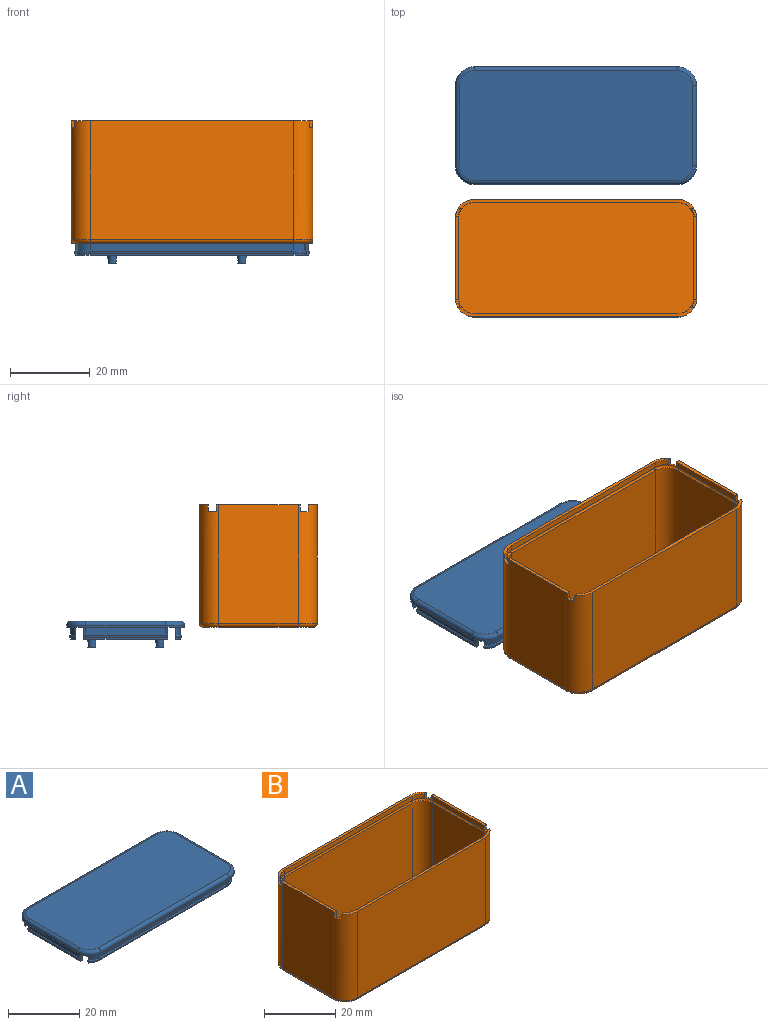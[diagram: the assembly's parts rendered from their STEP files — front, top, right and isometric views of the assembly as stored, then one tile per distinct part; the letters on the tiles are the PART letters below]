
ASSEMBLY  parts=2 mates=1
PART A: 82 faces, bbox 61.3x30.3x6.5 mm
  f0: torus R=3.75mm, axis (0,0,1), area 0.5mm2, adj f14,f15,f20,f68
  f1: torus R=3.75mm, axis (0,0,1), area 0.5mm2, adj f13,f16,f24,f67
  f2: torus R=3.75mm, axis (0,0,1), area 3.3mm2, adj f12,f17,f19,f65
  f3: torus R=3.75mm, axis (0,0,1), area 3.3mm2, adj f11,f18,f19,f62
  f4: cylinder r=3mm len=3mm, axis (0,0,1), area 1.5mm2, adj f10,f27,f50,f68
  f5: cylinder r=3mm len=3mm, axis (0,0,1), area 1.5mm2, adj f9,f31,f50,f67
  f6: cylinder r=3mm len=3mm, axis (0,0,1), area 5.3mm2, adj f8,f33,f50,f65
  f7: cylinder r=3mm len=3mm, axis (0,0,1), area 5.3mm2, adj f8,f33,f50,f62
  f8: plane 56.59x1.25mm, normal (0,0,-1), area 42mm2, adj f6,f7,f11,f12,f33,f38,f62,f65
  f9: plane 21x0.79mm, normal (0,0,-1), area 15.8mm2, adj f5,f13,f31,f32,f39,f40,f64,f67
  f10: plane 21x0.79mm, normal (0,0,-1), area 15.8mm2, adj f4,f14,f27,f34,f36,f37,f63,f68
  f11: cylinder r=3.75mm len=2.8mm, axis (0,0,1), area 1.4mm2, adj f3,f8,f38,f62
  f12: cylinder r=3.75mm len=2.8mm, axis (0,0,1), area 1.4mm2, adj f2,f8,f38,f65
  f13: cylinder r=3.75mm len=0.5mm, axis (0,0,1), area 0.2mm2, adj f1,f9,f40,f67
  f14: cylinder r=3.75mm len=0.5mm, axis (0,0,1), area 0.2mm2, adj f0,f10,f36,f68
  f15: cylinder r=3.75mm len=1.95mm, axis (0,0,1), area 1mm2, adj f0,f49,f50,f68
  f16: cylinder r=3.75mm len=1.95mm, axis (0,0,1), area 1mm2, adj f1,f50,f60,f67
  f17: cylinder r=3.75mm len=2.8mm, axis (0,0,1), area 6.2mm2, adj f2,f47,f50,f65
  f18: cylinder r=3.75mm len=2.8mm, axis (0,0,1), area 6.2mm2, adj f3,f47,f50,f62
  f19: cylinder r=0.3mm len=51mm, axis (1,0,0), area 48.1mm2, adj f2,f3,f38,f47
  f20: cylinder r=0.3mm len=20mm, axis (0,-1,0), area 18.8mm2, adj f0,f26,f36,f49
  f21: torus R=3.75mm, axis (0,0,1), area 3.3mm2, adj f22,f43,f44,f69
  f22: cylinder r=0.3mm len=51mm, axis (-1,0,0), area 48.1mm2, adj f21,f23,f42,f61
  f23: torus R=3.75mm, axis (0,0,1), area 3.3mm2, adj f22,f41,f45,f66
  f24: cylinder r=0.3mm len=20mm, axis (0,1,0), area 18.8mm2, adj f1,f25,f40,f60
  f25: torus R=3.75mm, axis (0,0,1), area 0.5mm2, adj f24,f39,f46,f64
  f26: torus R=3.75mm, axis (0,0,1), area 0.5mm2, adj f20,f37,f48,f63
  f27: plane 20x3mm, normal (1,0,0), area 60mm2, adj f4,f10,f34,f50
  f28: cylinder r=3mm len=3mm, axis (0,0,1), area 5.3mm2, adj f29,f35,f50,f69
  f29: plane 51x3mm, normal (0,-1,0), area 153mm2, adj f28,f30,f35,f50
  f30: cylinder r=3mm len=3mm, axis (0,0,1), area 5.3mm2, adj f29,f35,f50,f66
  f31: plane 20x3mm, normal (-1,0,0), area 60mm2, adj f5,f9,f32,f50
  f32: cylinder r=3mm len=3mm, axis (0,0,1), area 1.5mm2, adj f9,f31,f50,f64
  f33: plane 51x3mm, normal (0,1,0), area 153mm2, adj f6,f7,f8,f50
  f34: cylinder r=3mm len=3mm, axis (0,0,1), area 1.5mm2, adj f10,f27,f50,f63
  f35: plane 56.59x1.25mm, normal (0,0,-1), area 42mm2, adj f28,f29,f30,f41,f42,f43,f66,f69
  f36: plane 20x0.45mm, normal (-1,0,0), area 9mm2, adj f10,f14,f20,f37
  f37: cylinder r=3.75mm len=0.5mm, axis (0,0,1), area 0.2mm2, adj f10,f26,f36,f63
  f38: plane 51x0.45mm, normal (0,-1,0), area 22.9mm2, adj f8,f11,f12,f19
  f39: cylinder r=3.75mm len=0.5mm, axis (0,0,1), area 0.2mm2, adj f9,f25,f40,f64
  f40: plane 20x0.45mm, normal (1,0,0), area 9mm2, adj f9,f13,f24,f39
  f41: cylinder r=3.75mm len=2.8mm, axis (0,0,1), area 1.4mm2, adj f23,f35,f42,f66
  f42: plane 51x0.45mm, normal (0,1,0), area 22.9mm2, adj f22,f35,f41,f43
  f43: cylinder r=3.75mm len=2.8mm, axis (0,0,1), area 1.4mm2, adj f21,f35,f42,f69
  f44: cylinder r=3.75mm len=2.8mm, axis (0,0,1), area 6.2mm2, adj f21,f50,f61,f69
  f45: cylinder r=3.75mm len=2.8mm, axis (0,0,1), area 6.2mm2, adj f23,f50,f61,f66
  f46: cylinder r=3.75mm len=1.95mm, axis (0,0,1), area 1mm2, adj f25,f50,f60,f64
  f47: plane 51x1.95mm, normal (0,-1,0), area 99.5mm2, adj f17,f18,f19,f50
  f48: cylinder r=3.75mm len=1.95mm, axis (0,0,1), area 1mm2, adj f26,f49,f50,f63
  f49: plane 20x1.95mm, normal (-1,0,0), area 39mm2, adj f15,f20,f48,f50
  f50: plane 60.5x29.5mm, normal (0,0,-1), area 1640.1mm2, adj f4,f5,f6,f7,f15,f16,f17,f18
  f51: plane 51x0.5mm, normal (0,1,0), area 25.5mm2, adj f50,f52,f58,f78
  f52: cylinder r=4.75mm len=4.75mm, axis (0,0,-1), area 3.7mm2, adj f50,f51,f53,f76
  f53: plane 20x0.5mm, normal (-1,0,0), area 10mm2, adj f50,f52,f54,f74
  f54: cylinder r=4.75mm len=4.75mm, axis (0,0,-1), area 3.7mm2, adj f50,f53,f55,f75
  f55: plane 51x0.5mm, normal (0,-1,0), area 25.5mm2, adj f50,f54,f56,f77
  f56: cylinder r=4.75mm len=4.75mm, axis (0,0,-1), area 3.7mm2, adj f50,f55,f57,f79
  f57: plane 20x0.5mm, normal (1,0,0), area 10mm2, adj f50,f56,f58,f81
  f58: cylinder r=4.75mm len=4.75mm, axis (0,0,-1), area 3.7mm2, adj f50,f51,f57,f80
  f59: plane 58.5x27.5mm, normal (0,0,1), area 1596.7mm2, adj f74,f75,f76,f77,f78,f79,f80,f81
  f60: plane 20x1.95mm, normal (1,0,0), area 39mm2, adj f16,f24,f46,f50
  f61: plane 51x1.95mm, normal (0,1,0), area 99.5mm2, adj f22,f44,f45,f50
  f62: plane 3x1.53mm, normal (0,1,0), area 3.6mm2, adj f3,f7,f8,f11,f18,f50
  f63: plane 3x1.06mm, normal (0,-1,0), area 2.4mm2, adj f10,f26,f34,f37,f48,f50
  f64: plane 3x1.06mm, normal (0,-1,0), area 2.4mm2, adj f9,f25,f32,f39,f46,f50
  f65: plane 3x1.53mm, normal (0,1,0), area 3.6mm2, adj f2,f6,f8,f12,f17,f50
  f66: plane 3x1.53mm, normal (0,-1,0), area 3.6mm2, adj f23,f30,f35,f41,f45,f50
  f67: plane 3x1.06mm, normal (0,1,0), area 2.4mm2, adj f1,f5,f9,f13,f16,f50
  f68: plane 3x1.06mm, normal (0,1,0), area 2.4mm2, adj f0,f4,f10,f14,f15,f50
  f69: plane 3x1.53mm, normal (0,-1,0), area 3.6mm2, adj f21,f28,f35,f43,f44,f50
  f70: cone r=1.25mm half-angle=3deg, axis (0,0,1), area 35.2mm2, adj f50,f71
  f71: plane 1.98x1.98mm, normal (0,0,-1), area 3.1mm2, adj f70
  f72: cone r=1.25mm half-angle=3deg, axis (0,0,1), area 35.2mm2, adj f50,f73
  f73: plane 1.98x1.98mm, normal (0,0,-1), area 3.1mm2, adj f72
  f74: cylinder r=1mm len=20mm, axis (0,1,0), area 31.4mm2, adj f53,f59,f75,f76
  f75: torus R=3.75mm, axis (0,0,1), area 10.8mm2, adj f54,f59,f74,f77
  f76: torus R=3.75mm, axis (0,0,1), area 10.8mm2, adj f52,f59,f74,f78
  f77: cylinder r=1mm len=51mm, axis (-1,0,0), area 80.1mm2, adj f55,f59,f75,f79
  f78: cylinder r=1mm len=51mm, axis (1,0,0), area 80.1mm2, adj f51,f59,f76,f80
  f79: torus R=3.75mm, axis (0,0,1), area 10.8mm2, adj f56,f59,f77,f81
  f80: torus R=3.75mm, axis (0,0,1), area 10.8mm2, adj f58,f59,f78,f81
  f81: cylinder r=1mm len=20mm, axis (0,-1,0), area 31.4mm2, adj f57,f59,f79,f80
PART B: 62 faces, bbox 61.3x30.3x30.7 mm
  f0: cylinder r=3.95mm len=3.06mm, axis (0,0,1), area 5.2mm2, adj f6,f15,f28,f49
  f1: cylinder r=3.95mm len=1.49mm, axis (0,0,1), area 0.7mm2, adj f8,f9,f12,f51
  f2: cylinder r=3.95mm len=1.49mm, axis (0,0,1), area 0.7mm2, adj f7,f10,f26,f47
  f3: cylinder r=3.95mm len=3.06mm, axis (0,0,1), area 5.2mm2, adj f6,f15,f30,f43
  f4: cylinder r=4.75mm len=29.7mm, axis (0,0,1), area 218mm2, adj f8,f17,f18,f23,f51,f52,f53,f60
  f5: cylinder r=4.75mm len=29.7mm, axis (0,0,1), area 218mm2, adj f7,f17,f22,f23,f45,f46,f47,f56
  f6: plane 59.08x2.25mm, normal (0,0,1), area 47.5mm2, adj f0,f3,f15,f19,f20,f21,f43,f49
  f7: plane 21x0.83mm, normal (0,0,1), area 16.8mm2, adj f2,f5,f16,f21,f22,f26,f44,f47
  f8: plane 21x0.83mm, normal (0,0,1), area 16.8mm2, adj f1,f4,f11,f12,f18,f19,f48,f51
  f9: torus R=3.75mm, axis (0,0,1), area 6.8mm2, adj f1,f13,f27,f32,f39,f51,f52,f53
  f10: torus R=3.75mm, axis (0,0,1), area 6.8mm2, adj f2,f14,f27,f29,f37,f45,f46,f47
  f11: cylinder r=3.95mm len=1.49mm, axis (0,0,1), area 0.7mm2, adj f8,f12,f28,f48
  f12: plane 20x1.49mm, normal (1,0,0), area 29.9mm2, adj f1,f8,f11,f32
  f13: cylinder r=3.95mm len=3.06mm, axis (0,0,1), area 5.2mm2, adj f9,f23,f25,f52
  f14: cylinder r=3.95mm len=3.06mm, axis (0,0,1), area 5.2mm2, adj f10,f23,f25,f46
  f15: plane 51x1.49mm, normal (0,1,0), area 76.2mm2, adj f0,f3,f6,f31
  f16: cylinder r=3.95mm len=1.49mm, axis (0,0,1), area 0.7mm2, adj f7,f26,f30,f44
  f17: plane 51x29.7mm, normal (0,1,0), area 1514.7mm2, adj f4,f5,f23,f58
  f18: plane 29.7x20mm, normal (-1,0,0), area 594mm2, adj f4,f8,f19,f61
  f19: cylinder r=4.75mm len=29.7mm, axis (0,0,1), area 218mm2, adj f6,f8,f18,f20,f48,f49,f50,f59
  f20: plane 51x29.7mm, normal (0,-1,0), area 1514.7mm2, adj f6,f19,f21,f57
  f21: cylinder r=4.75mm len=29.7mm, axis (0,0,1), area 218mm2, adj f6,f7,f20,f22,f42,f43,f44,f55
  f22: plane 29.7x20mm, normal (1,0,0), area 594mm2, adj f5,f7,f21,f54
  f23: plane 59.08x2.25mm, normal (0,0,1), area 47.5mm2, adj f4,f5,f13,f14,f17,f25,f46,f52
  f24: plane 58.5x27.5mm, normal (0,0,-1), area 1596.7mm2, adj f54,f55,f56,f57,f58,f59,f60,f61
  f25: plane 51x1.49mm, normal (0,-1,0), area 76.2mm2, adj f13,f14,f23,f27
  f26: plane 20x1.49mm, normal (-1,0,0), area 29.9mm2, adj f2,f7,f16,f29
  f27: cylinder r=0.5mm len=51mm, axis (-1,0,0), area 58.8mm2, adj f9,f10,f25,f38
  f28: torus R=3.75mm, axis (0,0,1), area 6.8mm2, adj f0,f11,f31,f32,f41,f48,f49,f50
  f29: cylinder r=0.5mm len=20mm, axis (0,1,0), area 23.1mm2, adj f10,f26,f30,f34
  f30: torus R=3.75mm, axis (0,0,1), area 6.8mm2, adj f3,f16,f29,f31,f35,f42,f43,f44
  f31: cylinder r=0.5mm len=51mm, axis (1,0,0), area 58.8mm2, adj f15,f28,f30,f36
  f32: cylinder r=0.5mm len=20mm, axis (0,-1,0), area 23.1mm2, adj f9,f12,f28,f40
  f33: plane 58.9x27.9mm, normal (0,0,1), area 1629.9mm2, adj f34,f35,f36,f37,f38,f39,f40,f41
  f34: plane 27.29x20mm, normal (-1,0,0), area 545.9mm2, adj f29,f33,f35,f37
  f35: cylinder r=3.95mm len=27.29mm, axis (0,0,1), area 169.3mm2, adj f30,f33,f34,f36
  f36: plane 51x27.29mm, normal (0,1,0), area 1392mm2, adj f31,f33,f35,f41
  f37: cylinder r=3.95mm len=27.29mm, axis (0,0,1), area 169.3mm2, adj f10,f33,f34,f38
  f38: plane 51x27.29mm, normal (0,-1,0), area 1392mm2, adj f27,f33,f37,f39
  f39: cylinder r=3.95mm len=27.29mm, axis (0,0,1), area 169.3mm2, adj f9,f33,f38,f40
  f40: plane 27.29x20mm, normal (1,0,0), area 545.9mm2, adj f32,f33,f39,f41
  f41: cylinder r=3.95mm len=27.29mm, axis (0,0,1), area 169.3mm2, adj f28,f33,f36,f40
  f42: plane 2x1.37mm, normal (0,0,1), area 1.2mm2, adj f21,f30,f43,f44
  f43: plane 1.7x0.98mm, normal (0,1,0), area 1.6mm2, adj f3,f6,f21,f30,f42
  f44: plane 1.71x0.81mm, normal (0,-1,0), area 1.3mm2, adj f7,f16,f21,f30,f42
  f45: plane 2x1.37mm, normal (0,0,1), area 1.2mm2, adj f5,f10,f46,f47
  f46: plane 1.7x0.98mm, normal (0,-1,0), area 1.6mm2, adj f5,f10,f14,f23,f45
  f47: plane 1.71x0.81mm, normal (0,1,0), area 1.3mm2, adj f2,f5,f7,f10,f45
  f48: plane 1.71x0.81mm, normal (0,-1,0), area 1.3mm2, adj f8,f11,f19,f28,f50
  f49: plane 1.7x0.98mm, normal (0,1,0), area 1.6mm2, adj f0,f6,f19,f28,f50
  f50: plane 2x1.37mm, normal (0,0,1), area 1.2mm2, adj f19,f28,f48,f49
  f51: plane 1.71x0.81mm, normal (0,1,0), area 1.3mm2, adj f1,f4,f8,f9,f53
  f52: plane 1.7x0.98mm, normal (0,-1,0), area 1.6mm2, adj f4,f9,f13,f23,f53
  f53: plane 2x1.37mm, normal (0,0,1), area 1.2mm2, adj f4,f9,f51,f52
  f54: cylinder r=1mm len=20mm, axis (0,1,0), area 31.4mm2, adj f22,f24,f55,f56
  f55: torus R=3.75mm, axis (0,0,-1), area 10.8mm2, adj f21,f24,f54,f57
  f56: torus R=3.75mm, axis (0,0,-1), area 10.8mm2, adj f5,f24,f54,f58
  f57: cylinder r=1mm len=51mm, axis (1,0,0), area 80.1mm2, adj f20,f24,f55,f59
  f58: cylinder r=1mm len=51mm, axis (-1,0,0), area 80.1mm2, adj f17,f24,f56,f60
  f59: torus R=3.75mm, axis (0,0,-1), area 10.8mm2, adj f19,f24,f57,f61
  f60: torus R=3.75mm, axis (0,0,-1), area 10.8mm2, adj f4,f24,f58,f61
  f61: cylinder r=1mm len=20mm, axis (0,-1,0), area 31.4mm2, adj f18,f24,f59,f60
PLACE A t=(-0.02,0,-31)mm
PLACE B t=(0,-33.24,0)mm
MATE planar A.f50 <-> B.f24  axis (0,0,-1) through (0,0,-31)mm
